# Revit family: FU_Table_Sandler_Cono 4003
name_source: partatom
category: Furniture
units: mm (PartAtom-declared; Revit-internal decimal feet)

## family parameters
Always vertical = Yes
Cut with Voids When Loaded = No
OmniClass Number = 23.40.20.00
OmniClass Title = General Furniture and Specialties
Render Appearance Source = Family Geometry
Room Calculation Point = No
Shared = No
Work Plane-Based = No

## types (1)
- Cono 4003
    Default Elevation = 0 mm  [stored 0 ft]
    Depth = 310 mm  [stored 1.01706 ft]
    Description = Metal side table base at 55cm/21.75" high, available in pearl gold, black, or lacquered finishes. Maximum tabletop size: 80cm/32" diameter
    Height = 550 mm
    Manufacturer = Sandler
    Model = Cono 4003
    URL = https://www.sandlerseating.com
    Width = 310 mm  [stored 1.01706 ft]

note: [stored X ft] marks values corroborated as IEEE doubles in the binary element streams (Revit-internal decimal feet)

## geometry (parser evidence)
native form markers: Sweep x5
no freeform markers — native parametric forms only
